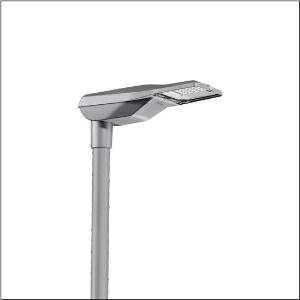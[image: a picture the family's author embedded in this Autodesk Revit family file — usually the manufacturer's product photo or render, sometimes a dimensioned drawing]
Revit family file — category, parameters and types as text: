
# Revit family: streetlight_sl_21_micro___st0_8a_5xe5c23a08cb_7bdd
name_source: partatom
category: Lighting Fixtures
units: mm (PartAtom-declared; Revit-internal decimal feet)

## family parameters
Cut with Voids When Loaded = No
Host = Face
Light Source = No
Part Type = Normal
Room Calculation Point = No
Round Connector Dimension = Use Diameter
Shared = No

## types (1)
- --- (1 x LED, 1900 lm, 15.8 W, 2200K)
    Apparent Load = 16 VA
    CIE Flux Codes = 38 75 97 100 100
    Color Rendering = 70
    Color Temperature = 2200K
    Default Elevation = 1800 mm
    Description = Streetlight SL 21 micro, mast luminaire, primary light control with lens, of PMMA, primary optical cover: cover, of toughened safety glass, transparent, light distribution: ST0.8a, light emission: direct distribution, primary light characteristic: asymmetric, installation type: side-entry, post-top, LED, 3G 1.5mm², High Power LED, rated luminous flux: 1.900lm, luminous efficacy: 120lm/W, light colour: 722, colour temperature: 2200K, control: flexible luminous flux parameterisation, time-dependent luminous flux control, constant luminous flux control, overheat protection, mains connection: 230..240V, AC, 50/60Hz, connection cable pre-assembled, cable length: 5,5m, wiring characteristics: H07RN-F, start of lifetime: 16W, end of service life: 16W, reduction: 8W, luminaire housing, of diecast aluminium, powder-coated, Siteco® metallic grey (DB 702S), corrosivity category C5 mid according to DIN EN ISO 12944, please order mast flange separately, inclination adjustable: 0°, 5°, 10°, 15°, sealing non-destructively replaceable, multi-level sealing system, length: 528mm, width: 235mm, height: 110mm, mast flange for spigot size: 42mm (side-entry): 5XC10008XM4, 60/48mm (side-entry/post-top): 5XC10108XM2, 76/60mm (side-entry/post-top): 5XC10108XM1, protection rating (complete): IP66, insulation class (complete): insulation class II (safety insulation), certification: CE, ENEC, ENEC+, VDE, impact resistance: IK09, permissible operating ambient temperature for outdoor applications: -40..+50°C, standard-compliant lighting for roads and squares, packaging unit: 1 piece

Light Distribution: ST0.8a
    Height = 110 mm
    Lamp = 1 x LED
    Lamp Light Flux = 1900 lm
    Lamp Power = 15.8 W
    Lamp count = 1
    Length = 528 mm
    Luminous efficacy = 120 lm/W
    Manufacturer = Siteco
    ModVariant = No
    Model = 5XE5C23A08CB
    Number of Poles = 1
    OnlyDefault = Yes
    Power Factor = 1
    Product Name = Streetlight SL 21 micro | ST0.8a
    Product group = mast luminaire | pylon top
    ProductGroupID = 6100
    Protection Class = Protection class II
    Protection Degree = IP 66
    RLX_Detail_Level = 1
    RLX_Emergency_Light_Flux = 0 lm
    RLX_Emergency_Type = 0
    RLX_Emergency_Type_DB = No
    RlxData = <blob elided: 98157 chars, md5=ecb1ac2e>
    Socket = socket
    Standby Power = 0 W
    System Light Flux = 1900 lm
    System Power = 16 W
    Type Comments = factory setting: luminous flux: 100 % | Output Level: 100 % | 300 mA
    Type Image = l_1006881.jpg
    URL = http://relux.com
    VarID = @adj_124657
    Voltage = 0 V
    Weight = 0.00 kg
    Width = 235 mm

## geometry (parser evidence)
native form markers: Blend x4, Sweep x12
no freeform markers — native parametric forms only
